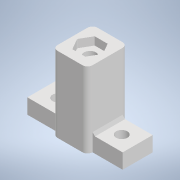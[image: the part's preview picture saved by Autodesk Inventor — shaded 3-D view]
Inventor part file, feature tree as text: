
AUTODESK INVENTOR PART (.ipt)
format: ipt  version: 2022 (Build 260153000, 153)  size: 194,048 bytes
history: native  units: mm
features: reference x24, sketch x5, extrude x4, other x4, hole x2, chamfer x1, fillet x1
ambient origin geometry x8: Origin, YZ Plane, XZ Plane, XY Plane, X Axis, Y Axis, Z Axis, Center Point
bodies: Solid1 (feature_tree)
feature tree (41):
  sketch  "Sketch1"  dims[d0=3.2512mm d1=3.2512mm]
  extrude  "Extrusion1"  Depth=3.2512mm
  extrude  "Extrusion3"  Depth=12.0mm
  chamfer  "Chamfer1"  Distance=6.0mm
  hole  "Hole1"  [1 undecoded]
  hole  "Hole2"  [1 undecoded]
  extrude  "Extrusion6"  Depth=2.0mm
  extrude  "Extrusion5"  Depth=2.0mm
  fillet  "Fillet1"  Radius=3.2mm
  sketch  "Sketch3"  dims[d3=0.0mm d4=12.0mm]
  sketch  "Sketch5"  dims[d6=38.1mm d8=6.0mm d9=0.0mm]
  sketch  "Sketch6"  dims[d12=10.0mm d14=0.0mm]
  sketch  "Sketch7"  dims[d16=24.13mm d17=0.0mm d18=3.0mm d19=2.0mm d20=45.0deg d21=4.7mm d22=8.0mm d23=4.0mm d24=2.0mm d25=90.0deg d26=11.8mm d27=20.594885mm d30=4.5mm d31=8.0mm d32=4.0mm d33=2.0mm d34=90.0deg d35=8.0mm d36=20.594885mm d37=6.35mm d38=6.35mm d39=3.2mm d40=0.0mm d41=2.0mm d42=2.0mm d43=2.0mm d44=2.0mm d45=8.0mm d46=0.0mm d49=2.0mm d50=0.1mm d51=0.1mm d52=0.1mm d53=0.1mm d54=0.1mm d55=0.1mm]
  reference  "Reference13"
  reference  "Reference14"
  reference  "Reference15"
  reference  "Reference16"
  reference  "Reference17"
  reference  "Reference18"
  reference  "Reference19"
  reference  "Reference20"
  reference  "Reference21"
  reference  "Reference22"
  reference  "Reference23"
  reference  "Reference24"
  reference  "Reference25"
  reference  "Reference26"
  reference  "Reference27"
  reference  "Reference28"
  reference  "Reference29"
  reference  "Reference30"
  reference  "Reference31"
  reference  "Reference32"
  reference  "Reference33"
  reference  "Reference34"
  reference  "Reference35"
  reference  "Reference36"
  other  "<userpath>\Desktop\P3 Bracket Files\Hopper Rest 8-32.iam"
  other  "Hopper Rest 8-32.iam"
  other  "BS EN 24032 - Metric M4:1"
  other  "8-32 Hex Nut:1"
note: 2 required parameter values undecoded (feature->parameter linkage not recoverable at this tier; creation-order binding heuristic only, values carry confidence <= 0.55)
